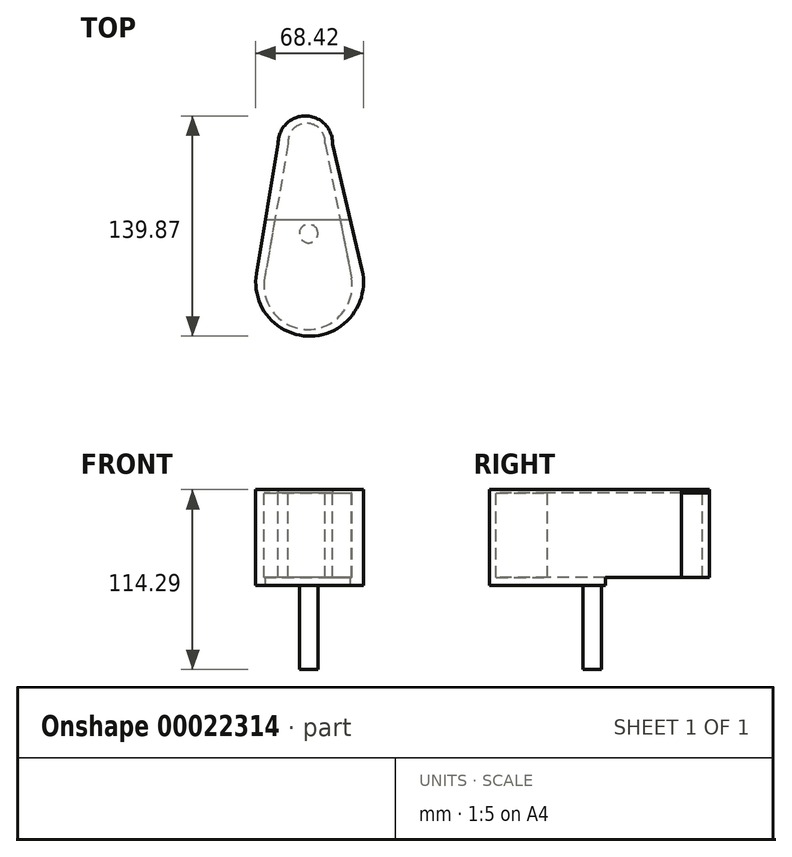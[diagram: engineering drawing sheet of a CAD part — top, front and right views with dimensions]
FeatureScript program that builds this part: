
annotation { "Feature Type Name" : "Feature", "Feature Type Description" : "" }
export const myFeature = defineFeature(function(context is Context, id is Id, definition is map)
    precondition{}
    {
        {
            var Q0;
            Q0=qCreatedBy(makeId("Top.planeOp"),FACE);
            var sketch = newSketch(context, id + "F0", { "sketchPlane" : qUnion([Q0])});
            skCircle(sketch, "E0", {"center": v(-10.1, 49.02) * mm, "radius": 17.26 * mm});
            skCircle(sketch, "E1", {"center": v(-7.43, -39.39) * mm, "radius": 34.2 * mm});
            skLineSegment(sketch, "E2", {"start": v(-27.37, 48.69) * mm, "end": v(-41.17, -33.74) * mm});
            skLineSegment(sketch, "E3", {"start": v(7.14, 48.45) * mm, "end": v(25.88, -31.6) * mm});
            skSolve(sketch);
        }
        {
            var Q0;
            Q0 = qSketchRegion(id + "F0", true);
            extrude(context, id + "F1", {"entities" : qUnion([Q0]), "depth" : 2.25 * mm});
        }
        {
            var Q0;
            Q0=makeQuery(id+"F1.opExtrude","CAP_FACE",FACE,{"disambiguationData":[OSD([sQuery(id+"F0.wireOp",EDGE,"E0"),sQuery(id+"F0.wireOp",EDGE,"E1"),sQuery(id+"F0.wireOp",EDGE,"E2"),sQuery(id+"F0.wireOp",EDGE,"E3")])],"isStart":false});
            var sketch = newSketch(context, id + "F2", { "sketchPlane" : qUnion([Q0])});
            skArc(sketch, "E4", {"start": v(7.14, 48.45) * mm, "mid": v(-10, 66) * mm, "end": v(-27.37, 48.69) * mm});
            skArc(sketch, "E5", {"start": v(2.35, 48.74) * mm, "mid": v(-9.42, 61.61) * mm, "end": v(-21.04, 48.61) * mm});
            skLineSegment(sketch, "E6", {"start": v(-21.04, 48.61) * mm, "end": v(-35.98, -36.49) * mm});
            skLineSegment(sketch, "E7", {"start": v(2.35, 48.74) * mm, "end": v(19.25, -36.77) * mm});
            skArc(sketch, "E8", {"start": v(-35.98, -36.49) * mm, "mid": v(-8.53, -69.34) * mm, "end": v(19.25, -36.77) * mm});
            skLineSegment(sketch, "E9", {"start": v(-27.37, 48.69) * mm, "end": v(-41.17, -33.74) * mm});
            skLineSegment(sketch, "E10", {"start": v(7.14, 48.45) * mm, "end": v(25.88, -31.6) * mm});
            skArc(sketch, "E11", {"start": v(-41.17, -33.74) * mm, "mid": v(-6.34, -73.58) * mm, "end": v(25.88, -31.6) * mm});
            skSolve(sketch);
        }
        {
            var Q0;
            Q0 = qSketchRegion(id + "F2", true);
            extrude(context, id + "F3", {"entities" : qUnion([Q0]), "operationType" : NewBodyOperationType.ADD, "oppositeDirection" : true, "depth" : 55.9 * mm});
        }
        {
            var Q0;
            Q0=makeQuery(id+"F3.opExtrude","CAP_FACE",FACE,{"disambiguationData":[OSD([sQuery(id+"F2.wireOp",EDGE,"E4"),sQuery(id+"F2.wireOp",EDGE,"E5"),sQuery(id+"F2.wireOp",EDGE,"E6"),sQuery(id+"F2.wireOp",EDGE,"E7"),sQuery(id+"F2.wireOp",EDGE,"E8"),sQuery(id+"F2.wireOp",EDGE,"E9"),sQuery(id+"F2.wireOp",EDGE,"E10"),sQuery(id+"F2.wireOp",EDGE,"E11")])],"isStart":false});
            var sketch = newSketch(context, id + "F4", { "sketchPlane" : qUnion([Q0])});
            skArc(sketch, "E12", {"start": v(25.88, 31.6) * mm, "mid": v(-6.34, 73.58) * mm, "end": v(-41.17, 33.74) * mm});
            skLineSegment(sketch, "E13", {"start": v(25.88, 31.6) * mm, "end": v(18.48, 0) * mm});
            skLineSegment(sketch, "E14", {"start": v(18.48, 0) * mm, "end": v(-35.52, 0) * mm});
            skLineSegment(sketch, "E15", {"start": v(-35.52, 0) * mm, "end": v(-41.17, 33.74) * mm});
            skSolve(sketch);
        }
        {
            var Q0;
            Q0 = qSketchRegion(id + "F4", true);
            extrude(context, id + "F5", {"entities" : qUnion([Q0]), "operationType" : NewBodyOperationType.ADD, "depth" : 5.08 * mm});
        }
        {
            var Q0;
            Q0=makeQuery(id+"F5.opExtrude","CAP_FACE",FACE,{"disambiguationData":[OSD([sQuery(id+"F4.wireOp",EDGE,"E12"),sQuery(id+"F4.wireOp",EDGE,"E13"),sQuery(id+"F4.wireOp",EDGE,"E14"),sQuery(id+"F4.wireOp",EDGE,"E15")])],"isStart":false});
            var sketch = newSketch(context, id + "F6", { "sketchPlane" : qUnion([Q0])});
            skCircle(sketch, "E16", {"center": v(-8.08, 8.4) * mm, "radius": 5.93 * mm});
            skSolve(sketch);
        }
        {
            var Q0;
            Q0 = qSketchRegion(id + "F6", true);
            extrude(context, id + "F7", {"entities" : qUnion([Q0]), "operationType" : NewBodyOperationType.ADD, "depth" : 53.31 * mm});
        }
    });
